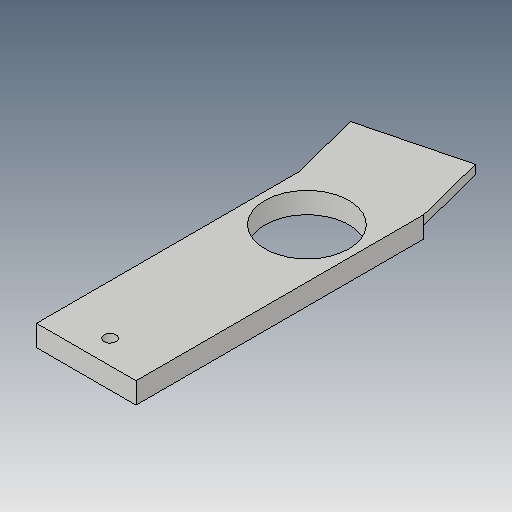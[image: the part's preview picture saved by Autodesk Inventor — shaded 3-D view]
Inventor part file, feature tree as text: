
AUTODESK INVENTOR PART (.ipt)
format: ipt  version: 2018.3 (Build 223284000, 284)  size: 129,024 bytes
history: native  units: in
note: dims shown in document units (in); Inventor stores cm internally (conversion verified against a paired STEP export)
features: extrude x3, sketch x3
ambient origin geometry x8: Origin, YZ Plane, XZ Plane, XY Plane, X Axis, Y Axis, Z Axis, Center Point
bodies: Solid1 (feature_tree)
feature tree (6):
  extrude  "Extrusion1"  Depth=0.221in TaperAngle=0.0deg
  extrude  "Extrusion4"  Depth=0.75in
  extrude  "Extrusion5"  Depth=0.125in
  sketch  "Sketch1"  dims[d4=0.88in d5=0.221in d6=0.0in]
  sketch  "Sketch4"  dims[d30=0.75in d32=0.75in]
  sketch  "Sketch5"  dims[d33=1.0429in d35=0.5215in d36=2.3125in d37=2.75in d38=0.126in d39=0.25in d40=1.0in d41=0.0in d42=0.52in d46=0.119in d47=0.1105in d48=0.125in d49=0.0in]
